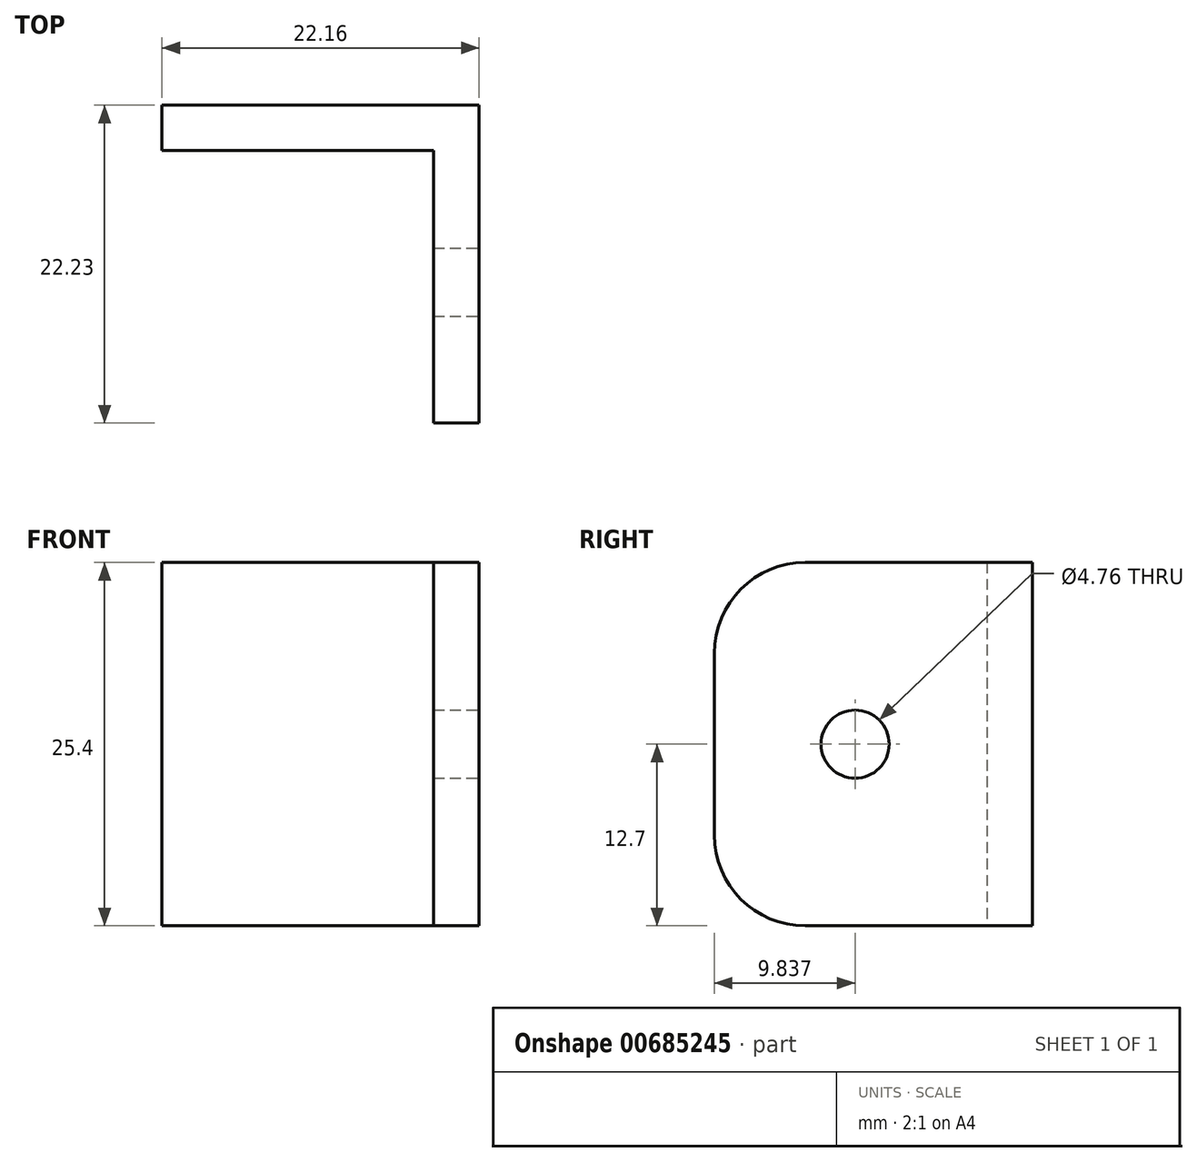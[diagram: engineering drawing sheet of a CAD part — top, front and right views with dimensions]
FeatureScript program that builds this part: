
annotation { "Feature Type Name" : "Feature", "Feature Type Description" : "" }
export const myFeature = defineFeature(function(context is Context, id is Id, definition is map)
    precondition{}
    {
        {
            var Q0;
            Q0=qCreatedBy(makeId("Front.planeOp"),FACE);
            var sketch = newSketch(context, id + "F0", { "sketchPlane" : qUnion([Q0])});
            skLineSegment(sketch, "E0.bottom", {"start": v(1.59, 12.7) * mm, "end": v(-1.59, 12.7) * mm});
            skLineSegment(sketch, "E0.top", {"start": v(1.59, -12.7) * mm, "end": v(-1.59, -12.7) * mm});
            skLineSegment(sketch, "E0.left", {"start": v(1.59, 12.7) * mm, "end": v(1.59, -12.7) * mm});
            skLineSegment(sketch, "E0.right", {"start": v(-1.59, 12.7) * mm, "end": v(-1.59, -12.7) * mm});
            skPoint(sketch, "E0.middle", {"position": v(0, 0) * mm});
            skSolve(sketch);
        }
        {
            var Q0;
            Q0 = qSketchRegion(id + "F0", true);
            extrude(context, id + "F1", {"entities" : qUnion([Q0]), "depth" : 19.05 * mm, "offsetDistance" : 25.4 * mm});
        }
        {
            var Q0;
            Q0=makeQuery(id+"F1.opExtrude","SWEPT_FACE",FACE,{"disambiguationData":[OSD([sQuery(id+"F0.wireOp",EDGE,"E0.left")])]});
            var sketch = newSketch(context, id + "F2", { "sketchPlane" : qUnion([Q0])});
            skPoint(sketch, "E1.visualSharp", {"position": v(-19.05, 12.7) * mm});
            skArc(sketch, "E1.filletArc", {"start": v(-12.7, 12.7) * mm, "mid": v(-17.2, 10.84) * mm, "end": v(-19.05, 6.35) * mm});
            skPoint(sketch, "E2.visualSharp", {"position": v(-19.05, -12.7) * mm});
            skArc(sketch, "E2.filletArc", {"start": v(-19.05, -6.35) * mm, "mid": v(-17.2, -10.84) * mm, "end": v(-12.7, -12.7) * mm});
            skLineSegment(sketch, "E3", {"start": v(-12.7, 12.7) * mm, "end": v(-19.05, 12.7) * mm});
            skLineSegment(sketch, "E4", {"start": v(-19.05, 6.35) * mm, "end": v(-19.05, 12.7) * mm});
            skLineSegment(sketch, "E5", {"start": v(-19.05, -6.35) * mm, "end": v(-19.05, -12.7) * mm});
            skLineSegment(sketch, "E6", {"start": v(-19.05, -12.7) * mm, "end": v(-12.7, -12.7) * mm});
            skCircle(sketch, "E7", {"center": v(-9.21, 0) * mm, "radius": 2.38 * mm});
            skSolve(sketch);
        }
        {
            var Q0;
            Q0 = qSketchRegion(id + "F2", true);
            extrude(context, id + "F3", {"entities" : qUnion([Q0]), "operationType" : NewBodyOperationType.REMOVE, "oppositeDirection" : true, "depth" : 25.4 * mm, "offsetDistance" : 25.4 * mm});
        }
        {
            var Q0;
            Q0=qCreatedBy(makeId("Right.planeOp"),FACE);
            var sketch = newSketch(context, id + "F4", { "sketchPlane" : qUnion([Q0])});
            skLineSegment(sketch, "E8.bottom", {"start": v(0, 12.7) * mm, "end": v(3.18, 12.7) * mm});
            skLineSegment(sketch, "E8.top", {"start": v(0, -12.7) * mm, "end": v(3.18, -12.7) * mm});
            skLineSegment(sketch, "E8.left", {"start": v(0, 12.7) * mm, "end": v(0, -12.7) * mm});
            skLineSegment(sketch, "E8.right", {"start": v(3.18, 12.7) * mm, "end": v(3.18, -12.7) * mm});
            skSolve(sketch);
        }
        {
            var Q0;
            Q0 = qSketchRegion(id + "F4", true);
            extrude(context, id + "F5", {"entities" : qUnion([Q0]), "operationType" : NewBodyOperationType.ADD, "oppositeDirection" : true, "depth" : 20.57 * mm, "offsetDistance" : 25.4 * mm, "hasSecondDirection" : true, "secondDirectionOppositeDirection" : false, "secondDirectionDepth" : 1.59 * mm});
        }
    });
